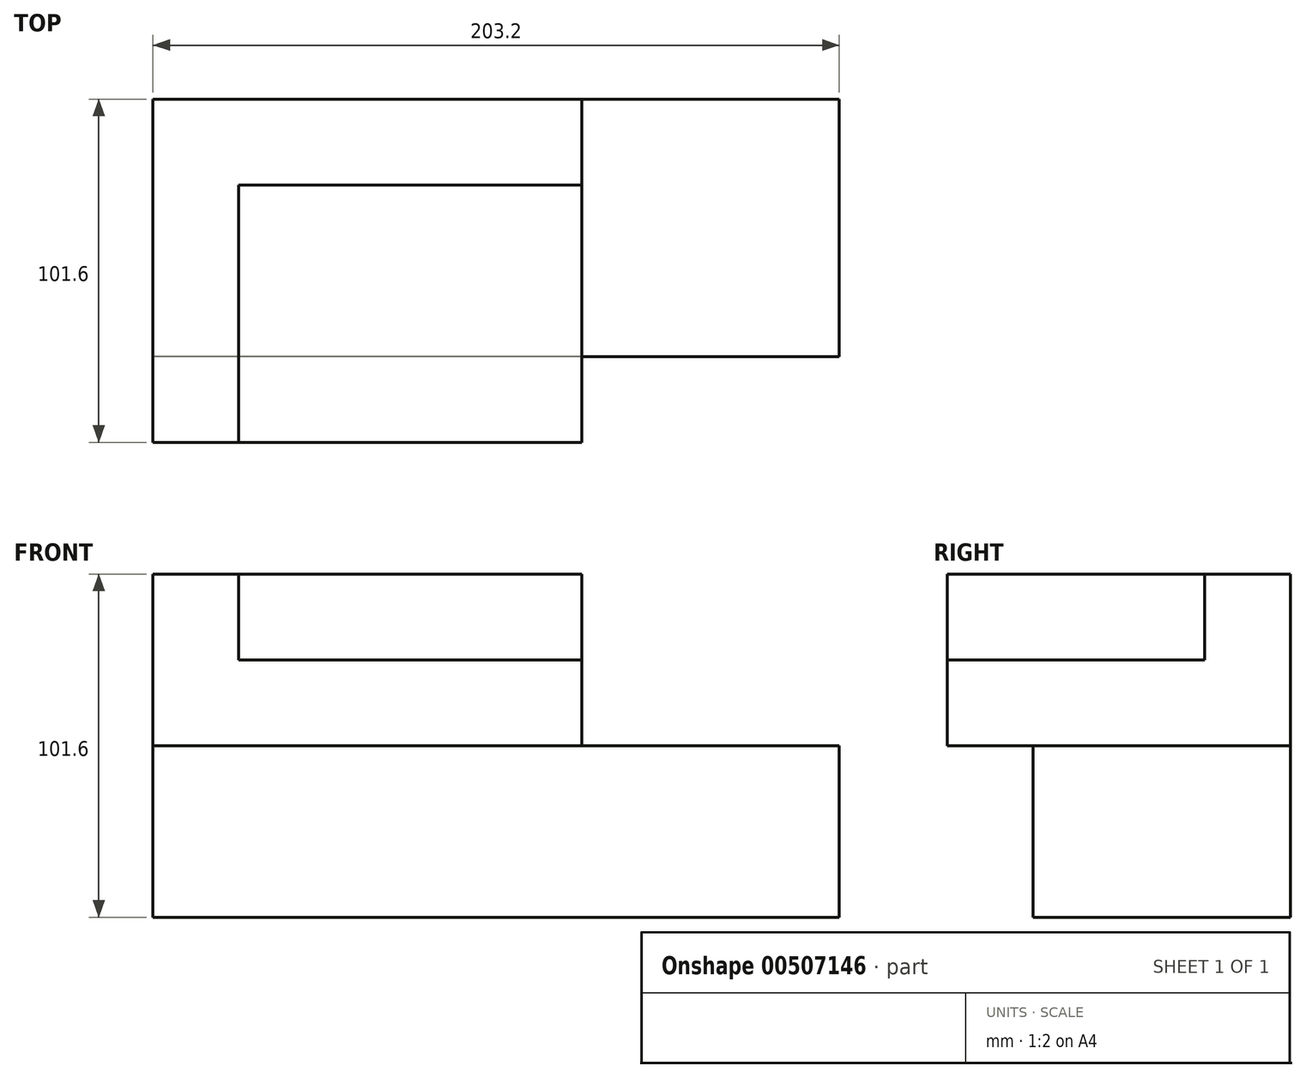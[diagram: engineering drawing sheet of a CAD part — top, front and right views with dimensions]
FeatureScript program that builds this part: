
annotation { "Feature Type Name" : "Feature", "Feature Type Description" : "" }
export const myFeature = defineFeature(function(context is Context, id is Id, definition is map)
    precondition{}
    {
        {
            var Q0;
            Q0=qCreatedBy(makeId("Front.planeOp"),FACE);
            var sketch = newSketch(context, id + "F0", { "sketchPlane" : qUnion([Q0])});
            skLineSegment(sketch, "E0.bottom", {"start": v(0, 0) * mm, "end": v(-203.2, 0) * mm});
            skLineSegment(sketch, "E0.top", {"start": v(0, 50.8) * mm, "end": v(-203.2, 50.8) * mm});
            skLineSegment(sketch, "E0.left", {"start": v(0, 0) * mm, "end": v(0, 50.8) * mm});
            skLineSegment(sketch, "E0.right", {"start": v(-203.2, 0) * mm, "end": v(-203.2, 50.8) * mm});
            skSolve(sketch);
        }
        {
            var Q0;
            Q0 = qSketchRegion(id + "F0", true);
            extrude(context, id + "F1", {"entities" : qUnion([Q0]), "depth" : 76.2 * mm});
        }
        {
            var Q0;
            Q0=qCreatedBy(makeId("Front.planeOp"),FACE);
            var sketch = newSketch(context, id + "F2", { "sketchPlane" : qUnion([Q0])});
            skLineSegment(sketch, "E1.bottom", {"start": v(-203.2, 50.8) * mm, "end": v(-76.2, 50.8) * mm});
            skLineSegment(sketch, "E1.top", {"start": v(-203.2, 101.6) * mm, "end": v(-76.2, 101.6) * mm});
            skLineSegment(sketch, "E1.left", {"start": v(-203.2, 50.8) * mm, "end": v(-203.2, 101.6) * mm});
            skLineSegment(sketch, "E1.right", {"start": v(-76.2, 50.8) * mm, "end": v(-76.2, 101.6) * mm});
            skSolve(sketch);
        }
        {
            var Q0;
            Q0=makeQuery(id+"F2.imprint","IMPRINT",FACE,{"disambiguationData":[TD([[makeQuery(id+"F2.imprint","IMPRINT",EDGE,{"derivedFrom":sQuery(id+"F2.wireOp",EDGE,"E1.bottom")}),1.0]])]});
            extrude(context, id + "F3", {"entities" : qUnion([Q0]), "operationType" : NewBodyOperationType.ADD, "depth" : 101.6 * mm});
        }
        {
            var Q0;
            Q0=makeQuery(id+"F3.opExtrude","CAP_FACE",FACE,{"disambiguationData":[OSD([sQuery(id+"F2.wireOp",EDGE,"E1.bottom"),sQuery(id+"F2.wireOp",EDGE,"E1.top"),sQuery(id+"F2.wireOp",EDGE,"E1.left"),sQuery(id+"F2.wireOp",EDGE,"E1.right")])],"isStart":false});
            var sketch = newSketch(context, id + "F4", { "sketchPlane" : qUnion([Q0])});
            skLineSegment(sketch, "E2.bottom", {"start": v(-76.2, 101.6) * mm, "end": v(-177.8, 101.6) * mm});
            skLineSegment(sketch, "E2.top", {"start": v(-76.2, 76.2) * mm, "end": v(-177.8, 76.2) * mm});
            skLineSegment(sketch, "E2.left", {"start": v(-76.2, 101.6) * mm, "end": v(-76.2, 76.2) * mm});
            skLineSegment(sketch, "E2.right", {"start": v(-177.8, 101.6) * mm, "end": v(-177.8, 76.2) * mm});
            skSolve(sketch);
        }
        {
            var Q0;
            Q0=makeQuery(id+"F4.imprint","IMPRINT",FACE,{"disambiguationData":[TD([[makeQuery(id+"F4.imprint","IMPRINT",EDGE,{"derivedFrom":sQuery(id+"F4.wireOp",EDGE,"E2.bottom")}),-1.0]])]});
            extrude(context, id + "F5", {"entities" : qUnion([Q0]), "operationType" : NewBodyOperationType.REMOVE, "oppositeDirection" : true, "depth" : 76.2 * mm});
        }
    });
